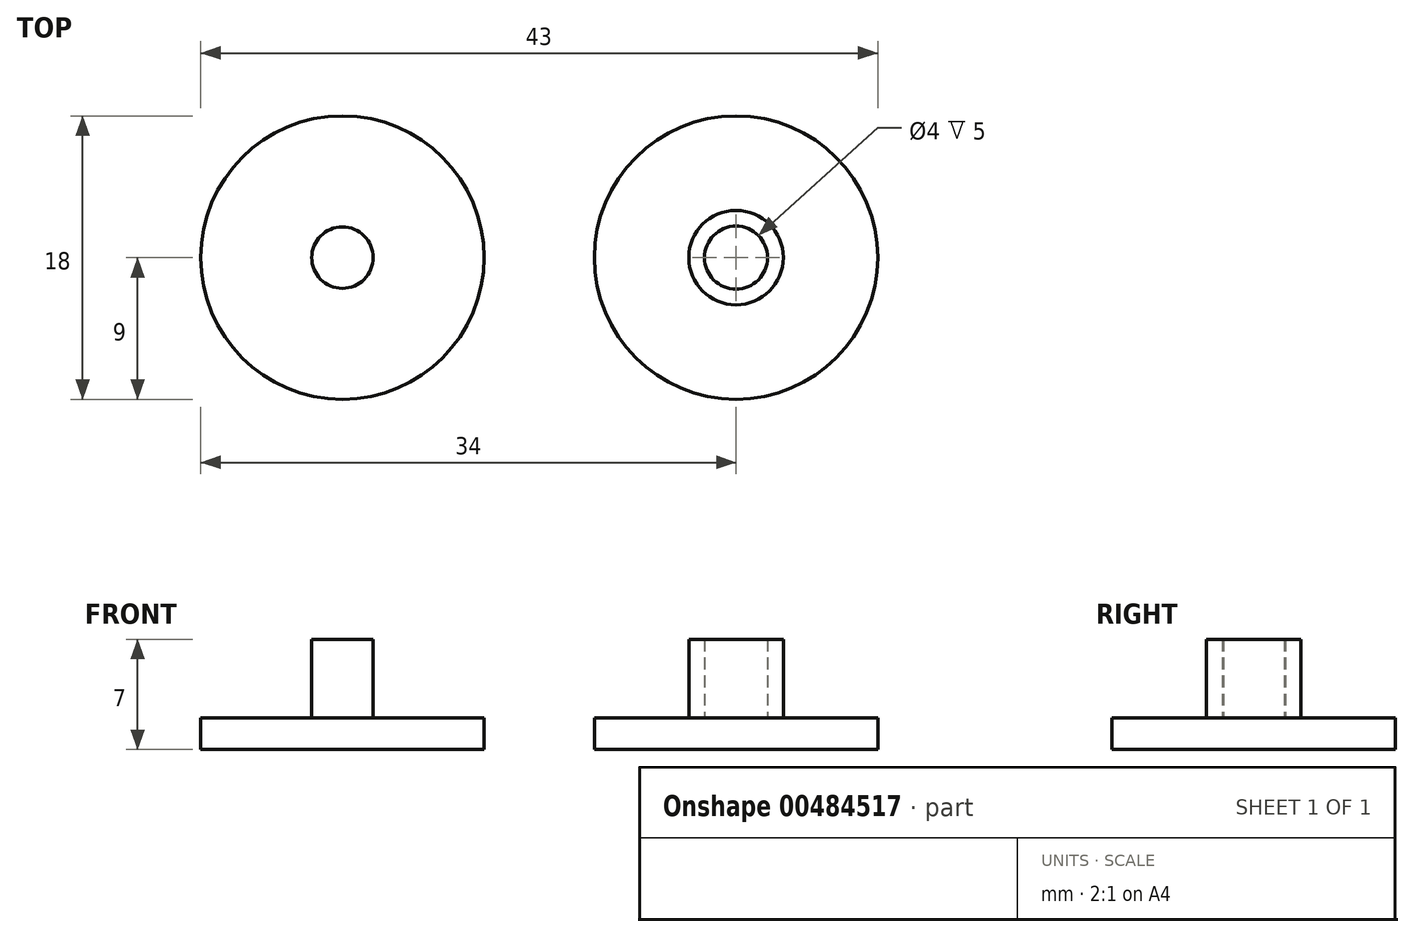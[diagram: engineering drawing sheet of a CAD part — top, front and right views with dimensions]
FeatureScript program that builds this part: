
annotation { "Feature Type Name" : "Feature", "Feature Type Description" : "" }
export const myFeature = defineFeature(function(context is Context, id is Id, definition is map)
    precondition{}
    {
        {
            var Q0;
            Q0=qCreatedBy(makeId("Top.planeOp"),FACE);
            var sketch = newSketch(context, id + "F0", { "sketchPlane" : qUnion([Q0])});
            skCircle(sketch, "E0", {"center": v(0, 0) * mm, "radius": 9 * mm});
            skCircle(sketch, "E1", {"center": v(-25, 0) * mm, "radius": 9 * mm});
            skSolve(sketch);
        }
        {
            var Q0;
            Q0=makeQuery(id+"F0.imprint","IMPRINT",FACE,{"disambiguationData":[TD([[makeQuery(id+"F0.imprint","IMPRINT",EDGE,{"derivedFrom":sQuery(id+"F0.wireOp",EDGE,"E0")}),1.0]])]});
            var Q1;
            Q1=makeQuery(id+"F0.imprint","IMPRINT",FACE,{"disambiguationData":[TD([[makeQuery(id+"F0.imprint","IMPRINT",EDGE,{"derivedFrom":sQuery(id+"F0.wireOp",EDGE,"E1")}),1.0]])]});
            extrude(context, id + "F1", {"entities" : qUnion([Q0, Q1]), "depth" : 2 * mm, "offsetDistance" : 25 * mm});
        }
        {
            var Q0;
            Q0=makeQuery(id+"F1.opExtrude","CAP_FACE",FACE,{"disambiguationData":[OSD([sQuery(id+"F0.wireOp",EDGE,"E0")])],"isStart":false});
            var sketch = newSketch(context, id + "F2", { "sketchPlane" : qUnion([Q0])});
            skCircle(sketch, "E2", {"center": v(0, 0) * mm, "radius": 3 * mm});
            skCircle(sketch, "E3", {"center": v(0, 0) * mm, "radius": 2 * mm});
            skSolve(sketch);
        }
        {
            var Q0;
            Q0 = qSketchRegion(id + "F2", true);
            extrude(context, id + "F3", {"entities" : qUnion([Q0]), "operationType" : NewBodyOperationType.ADD, "depth" : 5 * mm, "offsetDistance" : 25 * mm});
        }
        {
            var Q0;
            Q0=makeQuery(id+"F1.opExtrude","CAP_FACE",FACE,{"disambiguationData":[OSD([sQuery(id+"F0.wireOp",EDGE,"E1")])],"isStart":false});
            var sketch = newSketch(context, id + "F4", { "sketchPlane" : qUnion([Q0])});
            skCircle(sketch, "E4", {"center": v(-25, 0) * mm, "radius": 1.95 * mm});
            skSolve(sketch);
        }
        {
            var Q0;
            Q0=makeQuery(id+"F4.imprint","IMPRINT",FACE,{"disambiguationData":[TD([[makeQuery(id+"F4.imprint","IMPRINT",EDGE,{"derivedFrom":sQuery(id+"F4.wireOp",EDGE,"E4")}),1.0]])]});
            extrude(context, id + "F5", {"entities" : qUnion([Q0]), "operationType" : NewBodyOperationType.ADD, "depth" : 5 * mm, "offsetDistance" : 25 * mm});
        }
    });
